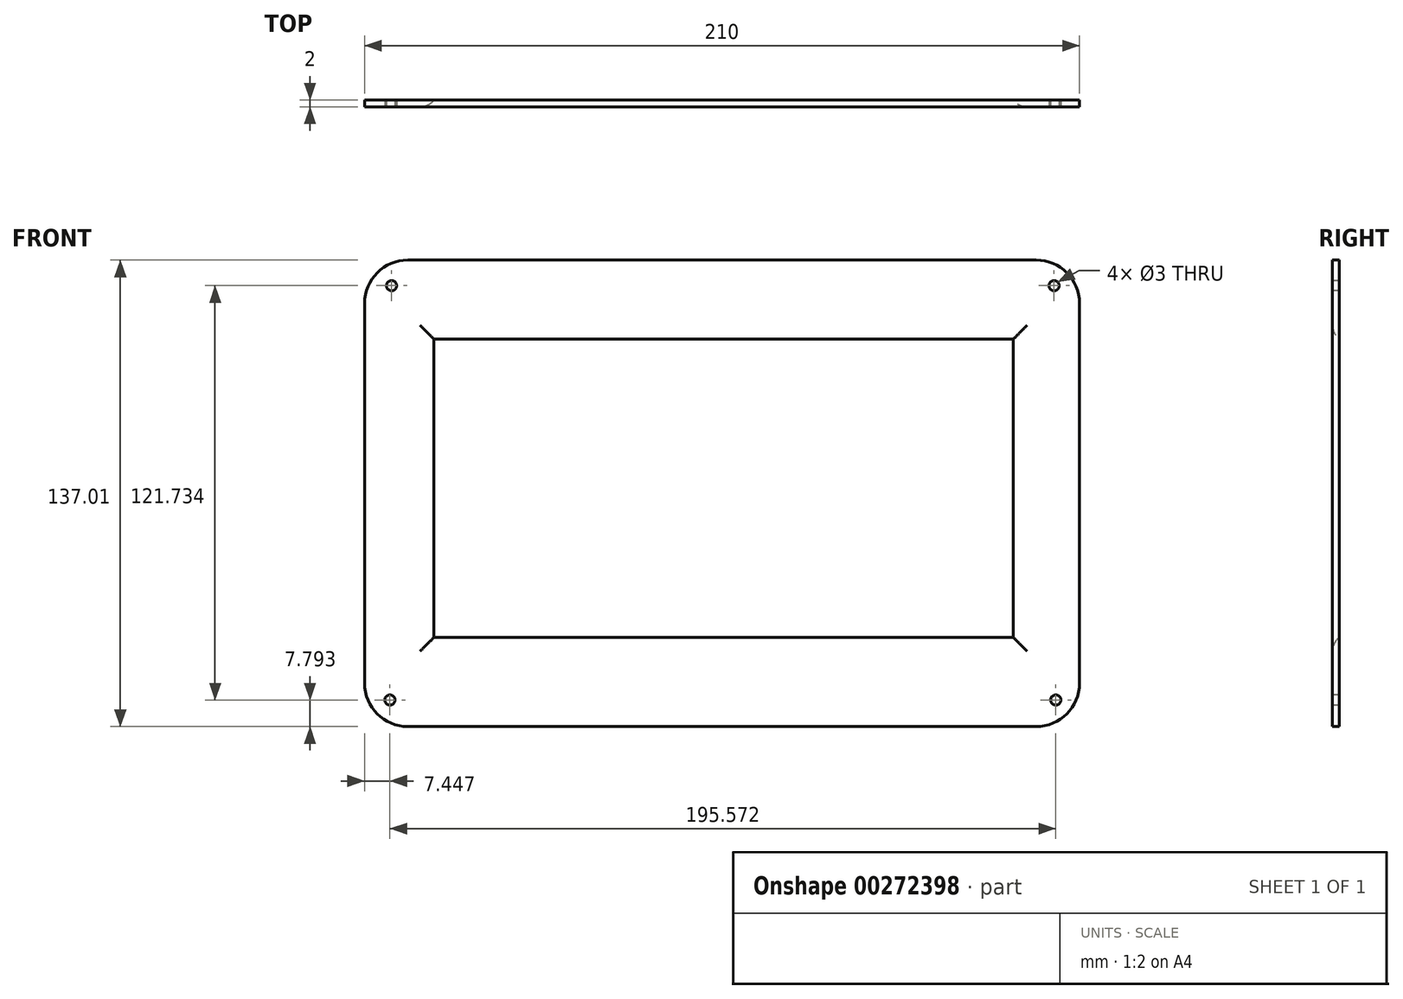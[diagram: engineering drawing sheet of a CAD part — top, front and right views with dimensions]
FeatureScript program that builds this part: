
annotation { "Feature Type Name" : "Feature", "Feature Type Description" : "" }
export const myFeature = defineFeature(function(context is Context, id is Id, definition is map)
    precondition{}
    {
        {
            var Q0;
            Q0=qCreatedBy(makeId("Front.planeOp"),FACE);
            var sketch = newSketch(context, id + "F0", { "sketchPlane" : qUnion([Q0])});
            skLineSegment(sketch, "E0.bottom", {"start": v(-82.6, 57.62) * mm, "end": v(87.58, 57.62) * mm});
            skLineSegment(sketch, "E0.top", {"start": v(-82.6, -30) * mm, "end": v(87.58, -30) * mm});
            skLineSegment(sketch, "E0.left", {"start": v(-82.6, 57.62) * mm, "end": v(-82.6, -30) * mm});
            skLineSegment(sketch, "E0.right", {"start": v(87.58, 57.62) * mm, "end": v(87.58, -30) * mm});
            skLineSegment(sketch, "E1.bottom", {"start": v(-90.29, 80.82) * mm, "end": v(94.31, 80.82) * mm});
            skLineSegment(sketch, "E1.top", {"start": v(-90.29, -56.19) * mm, "end": v(94.31, -56.19) * mm});
            skLineSegment(sketch, "E1.left", {"start": v(-102.99, 68.12) * mm, "end": v(-102.99, -43.49) * mm});
            skLineSegment(sketch, "E1.right", {"start": v(107.01, 68.12) * mm, "end": v(107.01, -43.49) * mm});
            skPoint(sketch, "E2.visualSharp", {"position": v(-102.99, 80.82) * mm});
            skArc(sketch, "E2.filletArc", {"start": v(-90.29, 80.82) * mm, "mid": v(-99.27, 77.1) * mm, "end": v(-102.99, 68.12) * mm});
            skPoint(sketch, "E3.visualSharp", {"position": v(-102.99, -56.19) * mm});
            skArc(sketch, "E3.filletArc", {"start": v(-102.99, -43.49) * mm, "mid": v(-99.27, -52.47) * mm, "end": v(-90.29, -56.19) * mm});
            skPoint(sketch, "E4.visualSharp", {"position": v(107.01, -56.19) * mm});
            skArc(sketch, "E4.filletArc", {"start": v(94.31, -56.19) * mm, "mid": v(103.3, -52.47) * mm, "end": v(107.01, -43.49) * mm});
            skPoint(sketch, "E5.visualSharp", {"position": v(107.01, 80.82) * mm});
            skArc(sketch, "E5.filletArc", {"start": v(107.01, 68.12) * mm, "mid": v(103.3, 77.1) * mm, "end": v(94.31, 80.82) * mm});
            skSolve(sketch);
        }
        {
            var Q0;
            Q0=makeQuery(id+"F0.imprint","IMPRINT",FACE,{"disambiguationData":[TD([[makeQuery(id+"F0.imprint","IMPRINT",EDGE,{"derivedFrom":sQuery(id+"F0.wireOp",EDGE,"E0.bottom")}),1.0]])]});
            extrude(context, id + "F1", {"entities" : qUnion([Q0]), "depth" : 2 * mm});
        }
        {
            var Q0;
            Q0=makeQuery(id+"F1.opExtrude","CAP_FACE",FACE,{"disambiguationData":[OSD([sQuery(id+"F0.wireOp",EDGE,"E0.bottom"),sQuery(id+"F0.wireOp",EDGE,"E0.top"),sQuery(id+"F0.wireOp",EDGE,"E0.left"),sQuery(id+"F0.wireOp",EDGE,"E0.right"),sQuery(id+"F0.wireOp",EDGE,"E1.bottom"),sQuery(id+"F0.wireOp",EDGE,"E1.top"),sQuery(id+"F0.wireOp",EDGE,"E1.left"),sQuery(id+"F0.wireOp",EDGE,"E1.right"),sQuery(id+"F0.wireOp",EDGE,"E2.filletArc"),sQuery(id+"F0.wireOp",EDGE,"E3.filletArc"),sQuery(id+"F0.wireOp",EDGE,"E4.filletArc"),sQuery(id+"F0.wireOp",EDGE,"E5.filletArc")])],"isStart":false});
            var sketch = newSketch(context, id + "F2", { "sketchPlane" : qUnion([Q0])});
            skCircle(sketch, "E6", {"center": v(-95.04, 73.34) * mm, "radius": 1.5 * mm});
            skCircle(sketch, "E7", {"center": v(-95.54, -48.4) * mm, "radius": 1.59 * mm});
            skCircle(sketch, "E8", {"center": v(100.03, -48.4) * mm, "radius": 1.7 * mm});
            skCircle(sketch, "E9", {"center": v(99.53, 73.34) * mm, "radius": 1.64 * mm});
            skSolve(sketch);
        }
        {
            var Q0;
            Q0=sQuery(id+"F2.wireOp",VERTEX,"E7.center");
            var Q1;
            Q1=sQuery(id+"F2.wireOp",VERTEX,"E6.center");
            var Q2;
            Q2=sQuery(id+"F2.wireOp",VERTEX,"E8.center");
            var Q3;
            Q3=sQuery(id+"F2.wireOp",VERTEX,"E9.center");
            var Q4;
            Q4=makeQuery(id+"F1.opExtrude","SWEPT_BODY",BODY,{"disambiguationData":[OSD([sQuery(id+"F0.wireOp",EDGE,"E0.bottom"),sQuery(id+"F0.wireOp",EDGE,"E0.top"),sQuery(id+"F0.wireOp",EDGE,"E0.left"),sQuery(id+"F0.wireOp",EDGE,"E0.right"),sQuery(id+"F0.wireOp",EDGE,"E1.bottom"),sQuery(id+"F0.wireOp",EDGE,"E1.top"),sQuery(id+"F0.wireOp",EDGE,"E1.left"),sQuery(id+"F0.wireOp",EDGE,"E1.right"),sQuery(id+"F0.wireOp",EDGE,"E2.filletArc"),sQuery(id+"F0.wireOp",EDGE,"E3.filletArc"),sQuery(id+"F0.wireOp",EDGE,"E4.filletArc"),sQuery(id+"F0.wireOp",EDGE,"E5.filletArc")])]});
            hole(context, id + "F3", {"style" : HoleStyle.SIMPLE, "endStyle" : HoleEndStyle.THROUGH, "holeDiameter" : 3 * mm, "tappedDepth" : 12.7 * mm, "tapClearance" : 3, "locations" : qUnion([Q0, Q1, Q2, Q3]), "scope" : qUnion([Q4])});
        }
        {
            var Q0;
            Q0=makeQuery(id+"F1.opExtrude","CAP_EDGE",EDGE,{"disambiguationData":[OSD([sQuery(id+"F0.wireOp",EDGE,"E0.right")])],"isStart":false});
            var Q1;
            Q1=makeQuery(id+"F1.opExtrude","CAP_EDGE",EDGE,{"disambiguationData":[OSD([sQuery(id+"F0.wireOp",EDGE,"E0.bottom")])],"isStart":false});
            var Q2;
            Q2=makeQuery(id+"F1.opExtrude","CAP_EDGE",EDGE,{"disambiguationData":[OSD([sQuery(id+"F0.wireOp",EDGE,"E0.left")])],"isStart":false});
            var Q3;
            Q3=makeQuery(id+"F1.opExtrude","CAP_EDGE",EDGE,{"disambiguationData":[OSD([sQuery(id+"F0.wireOp",EDGE,"E0.top")])],"isStart":false});
            fillet(context, id + "F4", {"entities" : qUnion([Q0, Q1, Q2, Q3]), "radius" : 5.08 * mm, "tangentPropagation" : true, "allowEdgeOverflow" : false});
        }
    });
